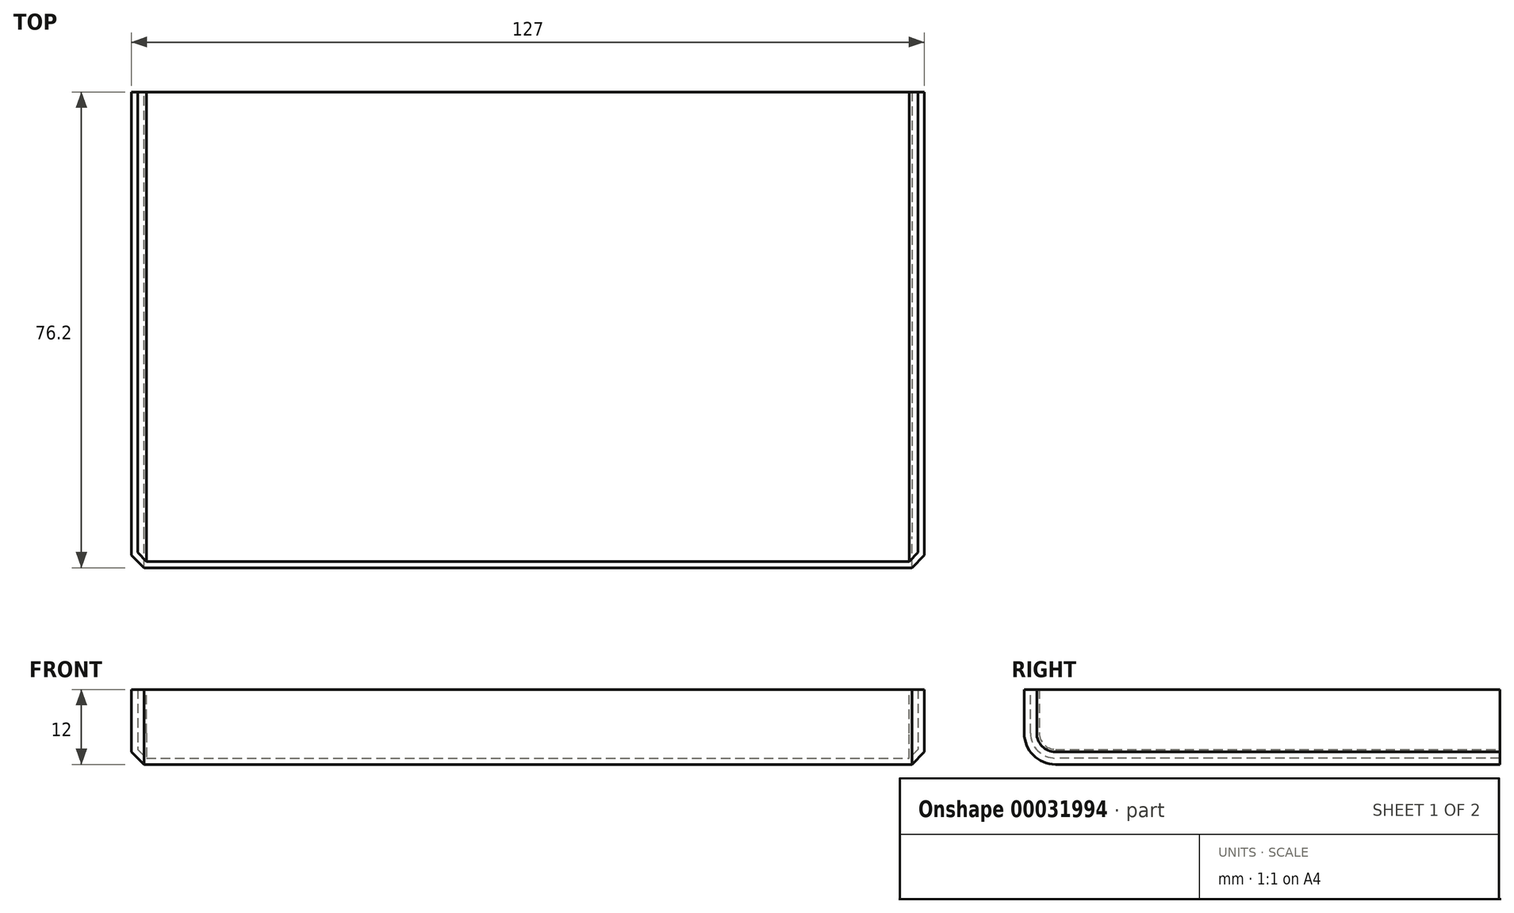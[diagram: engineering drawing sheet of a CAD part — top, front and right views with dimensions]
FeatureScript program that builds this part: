
annotation { "Feature Type Name" : "Feature", "Feature Type Description" : "" }
export const myFeature = defineFeature(function(context is Context, id is Id, definition is map)
    precondition{}
    {
        {
            var Q0;
            Q0=qCreatedBy(makeId("Top.planeOp"),FACE);
            var sketch = newSketch(context, id + "F0", { "sketchPlane" : qUnion([Q0])});
            skLineSegment(sketch, "E0.bottom", {"start": v(-127, 0) * mm, "end": v(0, 0) * mm});
            skLineSegment(sketch, "E0.top", {"start": v(-127, -76.2) * mm, "end": v(0, -76.2) * mm});
            skLineSegment(sketch, "E0.left", {"start": v(-127, 0) * mm, "end": v(-127, -76.2) * mm});
            skLineSegment(sketch, "E0.right", {"start": v(0, 0) * mm, "end": v(0, -76.2) * mm});
            skSolve(sketch);
        }
        {
            var Q0;
            Q0=makeQuery(id+"F0.imprint","IMPRINT",FACE,{"disambiguationData":[TD([[makeQuery(id+"F0.imprint","IMPRINT",EDGE,{"derivedFrom":sQuery(id+"F0.wireOp",EDGE,"E0.bottom")}),-1.0]])]});
            extrude(context, id + "F1", {"entities" : qUnion([Q0]), "depth" : 12 * mm});
        }
        {
            var Q0;
            Q0=makeQuery(id+"F1.opExtrude","CAP_EDGE",EDGE,{"disambiguationData":[OSD([sQuery(id+"F0.wireOp",EDGE,"E0.top")])],"isStart":true});
            fillet(context, id + "F2", {"entities" : qUnion([Q0]), "radius" : 5 * mm, "tangentPropagation" : true, "allowEdgeOverflow" : false});
        }
        {
            var Q0;
            Q0=makeQuery(id+"F1.opExtrude","SWEPT_EDGE",EDGE,{"disambiguationData":[OSD([sQuery(id+"F0.wireOp",EDGE,"E0.top"),sQuery(id+"F0.wireOp",EDGE,"E0.right")])]});
            var Q1;
            Q1=makeQuery(id+"F1.opExtrude","SWEPT_EDGE",EDGE,{"disambiguationData":[OSD([sQuery(id+"F0.wireOp",EDGE,"E0.top"),sQuery(id+"F0.wireOp",EDGE,"E0.left")])]});
            chamfer(context, id + "F3", {"entities" : qUnion([Q0, Q1]), "width" : 2 * mm, "tangentPropagation" : true});
        }
        {
            var Q0;
            Q0=makeQuery(id+"F1.opExtrude","CAP_FACE",FACE,{"disambiguationData":[OSD([sQuery(id+"F0.wireOp",EDGE,"E0.bottom"),sQuery(id+"F0.wireOp",EDGE,"E0.top"),sQuery(id+"F0.wireOp",EDGE,"E0.left"),sQuery(id+"F0.wireOp",EDGE,"E0.right")])],"isStart":false});
            var Q1;
            Q1=makeQuery(id+"F1.opExtrude","SWEPT_FACE",FACE,{"disambiguationData":[OSD([sQuery(id+"F0.wireOp",EDGE,"E0.bottom")])]});
            shell(context, id + "F4", {"entities" : qUnion([Q0, Q1]), "thickness" : 1 * mm});
        }
    });
